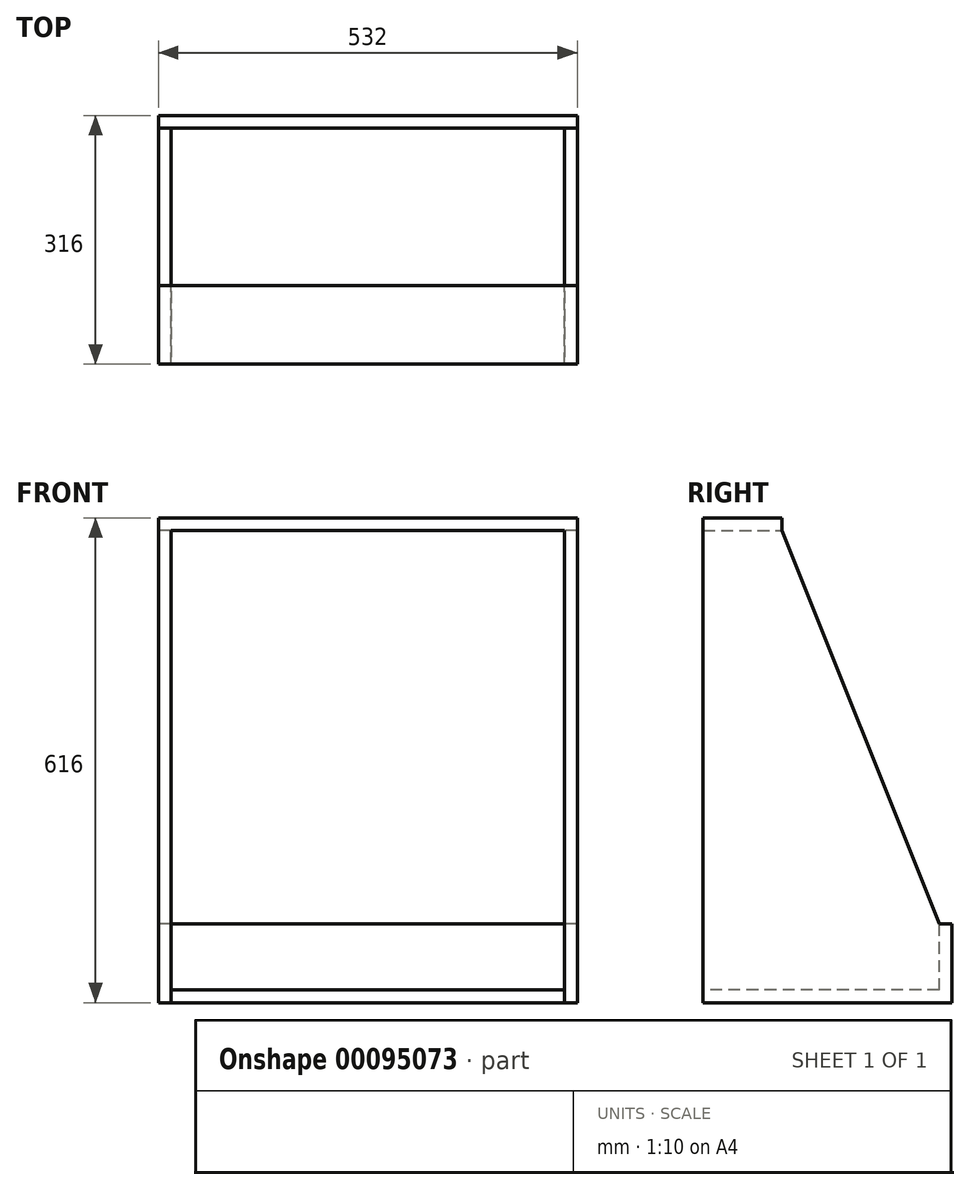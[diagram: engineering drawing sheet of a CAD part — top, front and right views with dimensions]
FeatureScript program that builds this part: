
annotation { "Feature Type Name" : "Feature", "Feature Type Description" : "" }
export const myFeature = defineFeature(function(context is Context, id is Id, definition is map)
    precondition{}
    {
        {
            var Q0;
            Q0=qCreatedBy(makeId("Top.planeOp"),FACE);
            var sketch = newSketch(context, id + "F0", { "sketchPlane" : qUnion([Q0])});
            skLineSegment(sketch, "E0.bottom", {"start": v(-250, 150) * mm, "end": v(250, 150) * mm});
            skLineSegment(sketch, "E0.top", {"start": v(-250, -150) * mm, "end": v(250, -150) * mm});
            skLineSegment(sketch, "E0.left", {"start": v(-250, 150) * mm, "end": v(-250, -150) * mm});
            skLineSegment(sketch, "E0.right", {"start": v(250, 150) * mm, "end": v(250, -150) * mm});
            skLineSegment(sketch, "E1", {"start": v(0, 150) * mm, "end": v(0, -150) * mm, "construction": true});
            skLineSegment(sketch, "E2", {"start": v(250, 0) * mm, "end": v(-250, 0) * mm, "construction": true});
            skSolve(sketch);
        }
        {
            var Q0;
            Q0 = qSketchRegion(id + "F0", true);
            var Q1;
            Q1=makeQuery(id+"F0.imprint","IMPRINT",FACE,{"disambiguationData":[TD([[makeQuery(id+"F0.imprint","IMPRINT",EDGE,{"derivedFrom":sQuery(id+"F0.wireOp",EDGE,"E0.bottom")}),-1.0]])]});
            extrude(context, id + "F1", {"entities" : qUnion([Q0, Q1]), "depth" : 16 * mm});
        }
        {
            var Q0;
            Q0=qCreatedBy(makeId("Right.planeOp"),FACE);
            var sketch = newSketch(context, id + "F2", { "sketchPlane" : qUnion([Q0])});
            skLineSegment(sketch, "E3.bottom", {"start": v(-150.03, 0) * mm, "end": v(149.97, 0) * mm});
            skLineSegment(sketch, "E3.top", {"start": v(-150.03, 100) * mm, "end": v(149.97, 100) * mm});
            skLineSegment(sketch, "E3.left", {"start": v(-150.03, 0) * mm, "end": v(-150.03, 100) * mm});
            skLineSegment(sketch, "E3.right", {"start": v(149.97, 0) * mm, "end": v(149.97, 100) * mm});
            skLineSegment(sketch, "E4", {"start": v(-150.03, 100) * mm, "end": v(-150.03, 600) * mm});
            skLineSegment(sketch, "E5", {"start": v(-150.03, 600) * mm, "end": v(-50.03, 600) * mm});
            skLineSegment(sketch, "E6", {"start": v(-50.03, 600) * mm, "end": v(-50.03, 100) * mm, "construction": true});
            skLineSegment(sketch, "E7", {"start": v(-50.03, 600) * mm, "end": v(149.97, 100) * mm});
            skSolve(sketch);
        }
        {
            var Q0;
            Q0=makeQuery(id+"F2.imprint","IMPRINT",FACE,{"disambiguationData":[TD([[makeQuery(id+"F2.imprint","IMPRINT",EDGE,{"derivedFrom":sQuery(id+"F2.wireOp",EDGE,"E3.top")}),1.0]])]});
            var Q1;
            Q1=makeQuery(id+"F2.imprint","IMPRINT",FACE,{"disambiguationData":[TD([[makeQuery(id+"F2.imprint","IMPRINT",EDGE,{"derivedFrom":sQuery(id+"F2.wireOp",EDGE,"E3.bottom")}),1.0]])]});
            extrude(context, id + "F3", {"entities" : qUnion([Q0, Q1]), "operationType" : NewBodyOperationType.ADD, "endBound" : BoundingType.SYMMETRIC, "depth" : 532 * mm});
        }
        {
            var Q0;
            Q0=makeQuery(id+"F3.opExtrude","SWEPT_FACE",FACE,{"disambiguationData":[OSD([sQuery(id+"F2.wireOp",EDGE,"E5")])]});
            extrude(context, id + "F4", {"entities" : qUnion([Q0]), "operationType" : NewBodyOperationType.ADD, "depth" : 16 * mm});
        }
        {
            var Q0;
            Q0 = qSketchRegion(id + "F2", true);
            extrude(context, id + "F5", {"entities" : qUnion([Q0]), "operationType" : NewBodyOperationType.REMOVE, "endBound" : BoundingType.SYMMETRIC, "oppositeDirection" : true, "depth" : 500 * mm});
        }
        {
            var Q0;
            Q0=makeQuery(id+"F0.imprint","IMPRINT",FACE,{"disambiguationData":[TD([[makeQuery(id+"F0.imprint","IMPRINT",EDGE,{"derivedFrom":sQuery(id+"F0.wireOp",EDGE,"E0.bottom")}),-1.0]])]});
            var Q1;
            Q1 = qConstructionFilter(qBodyType(qCreatedBy(id + "F0" ,EDGE), BodyType.WIRE), ConstructionObject.NO);
            extrude(context, id + "F6", {"entities" : qUnion([Q0]), "operationType" : NewBodyOperationType.ADD, "surfaceEntities" : qUnion([Q1]), "depth" : 16 * mm});
        }
        {
            var Q0;
            Q0=makeQuery(id+"F3.opExtrude","SWEPT_FACE",FACE,{"disambiguationData":[OSD([sQuery(id+"F2.wireOp",EDGE,"E3.right")])]});
            var sketch = newSketch(context, id + "F7", { "sketchPlane" : qUnion([Q0])});
            skLineSegment(sketch, "E8.bottom", {"start": v(-266, 100) * mm, "end": v(266, 100) * mm});
            skLineSegment(sketch, "E8.top", {"start": v(-266, 0) * mm, "end": v(266, 0) * mm});
            skLineSegment(sketch, "E8.left", {"start": v(-266, 100) * mm, "end": v(-266, 0) * mm});
            skLineSegment(sketch, "E8.right", {"start": v(266, 100) * mm, "end": v(266, 0) * mm});
            skSolve(sketch);
        }
        {
            var Q0;
            Q0 = qSketchRegion(id + "F7", true);
            extrude(context, id + "F8", {"entities" : qUnion([Q0]), "operationType" : NewBodyOperationType.ADD, "depth" : 16 * mm});
        }
    });
